# Revit family: ElectricalEquipment_Hager_Klik7Pin_LCM
name_source: partatom
category: Electrical Equipment
revit_build: Autodesk Revit 2015 (Build: 20160512_1515(x64)
units: mm (PartAtom-declared; Revit-internal decimal feet)

## types (2) — shared parameters
CE Approval = Yes
Colour = Aluminium / Light Grey
Default Elevation = 1200 mm
Design Country = China
Dual Switch Capability = Yes
Frequency = 50 Hz
Inflammability Rating = UL94 (V0)
Location of Manufacturer = Telford, TF1 7FT
MCB Rating = 10 A
Main Terminal Rating = 10 A
Mains Type = 1 phase
Manufacturer = Hager UK Ltd
Manufacturer Country = United Kingdom
Manufacturer Website = www.hager.co.uk
Material = Metal, Powder Coated, White
Neutral Rating = 100.00%
Outgoing Circuit Rating = 10 A
Overall Height = 58 mm  [stored 0.190289 ft]
Overall Width = 142 mm  [stored 0.465879 ft]
Packaging Recyclable = Yes
Packaging Weight = 0.10 kg
Product Family = Klik
Product Group = Klik
Reference Standard = BS 5733
Revision = 1
Shape = Rectangular
Supply Phase = 1
Terminal Capacity = 2 x 4mm2 CSA
Type = Lighting Control Module
URL = www.hager.co.uk
Voltage = 230
Warranty ID = Product Lifetime

## per-type parameters (varying)
| type | Description | EAN | Hager Catalogue Ref | Model | Number of Lighting Outlets | Product Description | Product Literature | Product Range | Product Weight |
| Klik LCM Marshalling Box 4 Channel 12W Pluggable | Klik Lighting Control Module 4 Channel 7 Pin 12W Pluggable | 5015654770419 | KLCM412P | KLCM412P | 12 | Klik Lighting Control Module 4 Channel 7 Pin 12W Pluggable | www.hager.co.uk/?artnr=KLCM412P | Klik Lighting Control Module 4 Channel 12W Pluggable | 2.10 kg |
| Klik LCM Marshalling Box 4 Channel 13W Hard Wired | Klik Lighting Control Module 4 Channel 7 Pin 13W Hard Wired | 5015654770426 | KLCM413W | KLCM413W | 13 | Klik Lighting Control Module 4 Channel 7 Pin 13W Hard Wired | www.hager.co.uk/?artnr=KLCM413W | Klik Lighting Control Module 4 Channel 13W Hard Wired | 2.50 kg |

note: [stored X ft] marks values corroborated as IEEE doubles in the binary element streams (Revit-internal decimal feet)

## geometry (parser evidence)
native form markers: Blend x4, Sweep x1
no freeform markers — native parametric forms only
